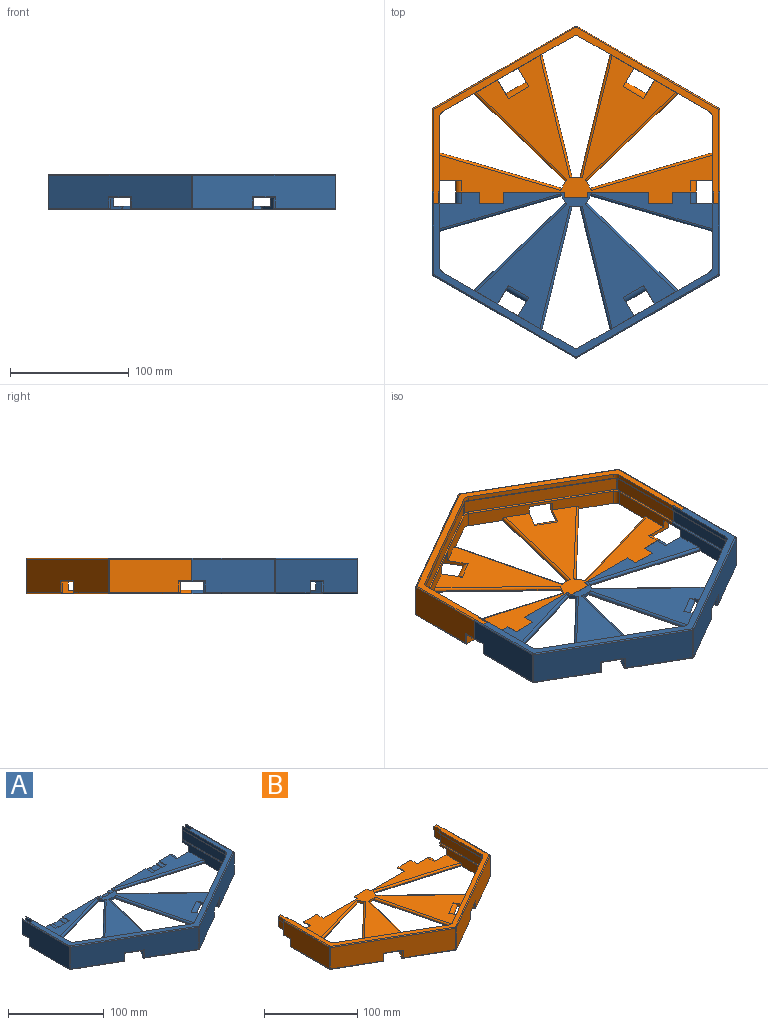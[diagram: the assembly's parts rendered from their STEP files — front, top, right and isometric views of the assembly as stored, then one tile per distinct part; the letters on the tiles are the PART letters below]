
ASSEMBLY  parts=2 mates=1
PART A: 155 faces, bbox 242.5x139.8x30 mm
  f0: plane 3.5x1.44mm, normal (0,0,1), area 1.1mm2, adj f121,f125,f126,f151
  f1: plane 3x2.31mm, normal (0,0,1), area 1.1mm2, adj f115,f122,f128,f153
  f2: plane 2.87x1.44mm, normal (0,0,-1), area 0.7mm2, adj f120,f125,f144
  f3: plane 2.5x2.08mm, normal (0,0,-1), area 0.7mm2, adj f114,f122,f146
  f4: plane 109.75x63.36mm, normal (0.5,0.87,0), area 1247.1mm2, adj f10,f14,f23,f28,f38,f39,f40,f133
  f5: plane 109.75x63.36mm, normal (-0.5,0.87,0), area 506.9mm2, adj f12,f129,f131,f145
  f6: plane 63.36x12.5mm, normal (1,0,0), area 623.6mm2, adj f7,f10,f14,f22,f36,f37,f133,f139
  f7: plane 20x6.5mm, normal (0,1,0), area 72.4mm2, adj f6,f12,f15,f18,f36,f49,f50,f51
  f8: plane 63.36x4mm, normal (-1,0,0), area 253.5mm2, adj f9,f12,f131,f147
  f9: plane 20x6.5mm, normal (0,1,0), area 72.4mm2, adj f8,f12,f16,f21,f34,f41,f42,f43
  f10: plane 229.5x114.89mm, normal (0,0,1), area 8571.3mm2, adj f4,f6,f11,f17,f21,f24,f27,f30
  f11: plane 202.49x3mm, normal (0,1,0), area 509.8mm2, adj f10,f14,f57,f58,f59,f60,f61,f62
  f12: plane 240.49x138.85mm, normal (0,0,1), area 2150.8mm2, adj f5,f7,f8,f9,f13,f15,f47,f48
  f13: plane 109.75x63.36mm, normal (0.5,0.87,0), area 506.9mm2, adj f12,f129,f130,f143
  f14: plane 240.49x138.85mm, normal (0,0,-1), area 12534mm2, adj f4,f6,f11,f17,f21,f22,f23,f24
  f15: plane 63.36x4mm, normal (1,0,0), area 253.5mm2, adj f7,f12,f130,f141
  f16: plane 69.42x28mm, normal (1,0,0), area 1833.8mm2, adj f9,f81,f82,f84,f90,f91
  f17: plane 109.75x63.36mm, normal (-0.5,0.87,0), area 1247.2mm2, adj f10,f14,f26,f29,f31,f32,f33,f132
  f18: plane 69.42x28mm, normal (-1,0,0), area 1833.8mm2, adj f7,f83,f85,f87,f88,f89
  f19: plane 120.24x69.42mm, normal (-0.5,-0.87,0), area 3667.7mm2, adj f88,f97,f98,f101,f104,f105,f107,f109
  f20: plane 120.24x69.42mm, normal (0.5,-0.87,0), area 3667.7mm2, adj f91,f92,f96,f99,f100,f103,f105,f106
  f21: plane 63.36x12.5mm, normal (-1,0,0), area 623.6mm2, adj f9,f10,f14,f25,f34,f35,f132,f136
  f22: plane 102.67x29.89mm, normal (0.28,-0.96,0), area 106.9mm2, adj f6,f14,f24,f139
  f23: plane 77.22x73.97mm, normal (-0.69,0.72,0), area 106.9mm2, adj f4,f14,f24,f140
  f24: plane 9.17x5.29mm, normal (-0.87,-0.5,0), area 21.2mm2, adj f10,f14,f22,f23,f139,f140
  f25: plane 102.67x29.89mm, normal (-0.28,-0.96,0), area 106.9mm2, adj f14,f21,f27,f136
  f26: plane 77.22x73.98mm, normal (0.69,0.72,0), area 106.9mm2, adj f14,f17,f27,f135
  f27: plane 9.17x5.29mm, normal (0.87,-0.5,0), area 21.2mm2, adj f10,f14,f25,f26,f135,f136
  f28: plane 103.86x25.46mm, normal (0.97,-0.24,0), area 106.9mm2, adj f4,f14,f30,f137
  f29: plane 103.86x25.46mm, normal (-0.97,-0.24,0), area 106.9mm2, adj f14,f17,f30,f138
  f30: plane 10.59x3mm, normal (0,-1,0), area 21.2mm2, adj f10,f14,f28,f29,f137,f138
  f31: plane 20.07x14.76mm, normal (0,0,-1), area 109.9mm2, adj f17,f32,f33,f100
  f32: plane 20.42x11.79mm, normal (0.87,0.5,0), area 99.3mm2, adj f10,f14,f17,f31,f103,f113
  f33: plane 20.42x11.79mm, normal (-0.87,-0.5,0), area 99.3mm2, adj f10,f14,f17,f31,f96,f113
  f34: plane 10x5.5mm, normal (0,0,-1), area 55mm2, adj f9,f21,f35,f81
  f35: plane 23.58x10mm, normal (0,1,0), area 99.3mm2, adj f10,f14,f21,f34,f82,f112
  f36: plane 10x5.5mm, normal (0,0,-1), area 55mm2, adj f6,f7,f37,f83
  f37: plane 23.58x10mm, normal (0,1,0), area 99.3mm2, adj f6,f10,f14,f36,f85,f111
  f38: plane 20.07x14.76mm, normal (0,0,-1), area 109.9mm2, adj f4,f39,f40,f104
  f39: plane 20.42x11.79mm, normal (0.87,-0.5,0), area 99.3mm2, adj f4,f10,f14,f38,f101,f110
  f40: plane 20.42x11.79mm, normal (-0.87,0.5,0), area 99.3mm2, adj f4,f10,f14,f38,f107,f110
  f41: plane 10x4.5mm, normal (-1,0,0), area 45mm2, adj f9,f42,f48,f90
  f42: plane 10x1mm, normal (0,0,1), area 10mm2, adj f9,f41,f43,f48
  f43: plane 10x10mm, normal (-1,0,0), area 100mm2, adj f9,f42,f44,f48
  f44: plane 10x2.5mm, normal (0,0,1), area 25mm2, adj f9,f43,f45,f48
  f45: plane 10x10mm, normal (1,0,0), area 100mm2, adj f9,f44,f46,f48
  f46: plane 10x1mm, normal (0,0,1), area 10mm2, adj f9,f45,f47,f48
  f47: plane 10x4.5mm, normal (1,0,0), area 45mm2, adj f9,f12,f46,f48
  f48: plane 14.5x4.5mm, normal (0,1,0), area 45.2mm2, adj f12,f41,f42,f43,f44,f45,f46,f47
  f49: plane 10x4.5mm, normal (-1,0,0), area 45mm2, adj f7,f12,f50,f56
  f50: plane 10x1mm, normal (0,0,1), area 10mm2, adj f7,f49,f51,f56
  f51: plane 10x10mm, normal (-1,0,0), area 100mm2, adj f7,f50,f52,f56
  f52: plane 10x2.5mm, normal (0,0,1), area 25mm2, adj f7,f51,f53,f56
  f53: plane 10x10mm, normal (1,0,0), area 100mm2, adj f7,f52,f54,f56
  f54: plane 10x1mm, normal (0,0,1), area 10mm2, adj f7,f53,f55,f56
  f55: plane 10x4.5mm, normal (1,0,0), area 45mm2, adj f7,f54,f56,f89
  f56: plane 14.5x4.5mm, normal (0,1,0), area 45.2mm2, adj f12,f49,f50,f51,f52,f53,f54,f55
  f57: plane 10x5mm, normal (0,0,1), area 50mm2, adj f11,f58,f63,f64
  f58: plane 10x1mm, normal (1,0,0), area 10mm2, adj f10,f11,f57,f64
  f59: plane 10x1mm, normal (-1,0,0), area 10mm2, adj f10,f11,f60,f64
  f60: plane 10x5mm, normal (0,0,1), area 50mm2, adj f11,f59,f61,f64
  f61: plane 10x1mm, normal (-1,0,0), area 10mm2, adj f11,f60,f62,f64
  f62: plane 10x10mm, normal (0,0,1), area 100mm2, adj f11,f61,f63,f64
  f63: plane 10x1mm, normal (1,0,0), area 10mm2, adj f11,f57,f62,f64
  f64: plane 20x2mm, normal (0,1,0), area 30mm2, adj f10,f57,f58,f59,f60,f61,f62,f63
  f65: plane 10x1mm, normal (-1,0,0), area 10mm2, adj f10,f11,f66,f72
  f66: plane 10x5mm, normal (0,0,1), area 50mm2, adj f11,f65,f67,f72
  f67: plane 10x1mm, normal (-1,0,0), area 10mm2, adj f11,f66,f68,f72
  f68: plane 10x10mm, normal (0,0,1), area 100mm2, adj f11,f67,f69,f72
  f69: plane 10x1mm, normal (1,0,0), area 10mm2, adj f11,f68,f70,f72
  f70: plane 10x5mm, normal (0,0,1), area 50mm2, adj f11,f69,f71,f72
  f71: plane 10x1mm, normal (1,0,0), area 10mm2, adj f10,f11,f70,f72
  f72: plane 20x2mm, normal (0,1,0), area 30mm2, adj f10,f65,f66,f67,f68,f69,f70,f71
  f73: plane 10x5mm, normal (0,0,1), area 50mm2, adj f11,f74,f79,f80
  f74: plane 5x1mm, normal (1,0,0), area 5mm2, adj f11,f73,f75,f80
  f75: plane 5x5mm, normal (0,0,1), area 25mm2, adj f11,f74,f76,f80
  f76: plane 5x1mm, normal (1,0,0), area 5mm2, adj f10,f11,f75,f80
  f77: plane 5x1mm, normal (-1,0,0), area 5mm2, adj f10,f11,f78,f80
  f78: plane 5x5mm, normal (0,0,1), area 25mm2, adj f11,f77,f79,f80
  f79: plane 5x1mm, normal (-1,0,0), area 5mm2, adj f11,f73,f78,f80
  f80: plane 20x2mm, normal (0,1,0), area 30mm2, adj f10,f73,f74,f75,f76,f77,f78,f79
  f81: cylinder r=1mm len=11mm, axis (0,-1,0), area 16.3mm2, adj f9,f16,f34,f82
  f82: cylinder r=1mm len=11mm, axis (0,0,-1), area 15.7mm2, adj f16,f35,f81,f84
  f83: cylinder r=1mm len=11mm, axis (0,1,0), area 16.3mm2, adj f7,f18,f36,f85
  f84: cylinder r=1mm len=59.42mm, axis (0,1,0), area 92.8mm2, adj f14,f16,f82,f86
  f85: cylinder r=1mm len=11mm, axis (0,0,1), area 15.7mm2, adj f18,f37,f83,f87
  f86: sphere r=1mm, area 1mm2, adj f84,f91,f92
  f87: cylinder r=1mm len=59.42mm, axis (0,-1,0), area 92.8mm2, adj f14,f18,f85,f93
  f88: cylinder r=1mm len=28mm, axis (0,0,-1), area 29.3mm2, adj f18,f19,f93,f94
  f89: cylinder r=1mm len=69.42mm, axis (0,1,0), area 109mm2, adj f7,f12,f18,f55,f94
  f90: cylinder r=1mm len=69.42mm, axis (0,-1,0), area 109mm2, adj f9,f12,f16,f41,f95
  f91: cylinder r=1mm len=28mm, axis (0,0,-1), area 29.3mm2, adj f16,f20,f86,f95
  f92: cylinder r=1mm len=51.96mm, axis (0.87,0.5,0), area 92.8mm2, adj f14,f20,f86,f96
  f93: sphere r=1mm, area 1mm2, adj f87,f88,f97
  f94: sphere r=1mm, area 1mm2, adj f88,f89,f98
  f95: sphere r=1mm, area 1mm2, adj f90,f91,f99
  f96: cylinder r=1mm len=11mm, axis (0,0,1), area 15.7mm2, adj f20,f33,f92,f100
  f97: cylinder r=1mm len=51.96mm, axis (0.87,-0.5,0), area 92.8mm2, adj f14,f19,f93,f101
  f98: cylinder r=1mm len=120.74mm, axis (-0.87,0.5,0), area 218.1mm2, adj f12,f19,f94,f102
  f99: cylinder r=1mm len=120.74mm, axis (-0.87,-0.5,0), area 218.1mm2, adj f12,f20,f95,f102
  f100: cylinder r=1mm len=19.55mm, axis (-0.87,-0.5,0), area 32.6mm2, adj f20,f31,f96,f103
  f101: cylinder r=1mm len=11mm, axis (0,0,-1), area 15.7mm2, adj f19,f39,f97,f104
  f102: sphere r=1mm, area 1mm2, adj f98,f99,f105
  f103: cylinder r=1mm len=11mm, axis (0,0,-1), area 15.7mm2, adj f20,f32,f100,f106
  f104: cylinder r=1mm len=19.55mm, axis (-0.87,0.5,0), area 32.6mm2, adj f19,f38,f101,f107
  f105: cylinder r=1mm len=28mm, axis (0,0,-1), area 29.3mm2, adj f19,f20,f102,f108
  f106: cylinder r=1mm len=51.96mm, axis (0.87,0.5,0), area 92.8mm2, adj f14,f20,f103,f108
  f107: cylinder r=1mm len=11mm, axis (0,0,1), area 15.7mm2, adj f19,f40,f104,f109
  f108: sphere r=1mm, area 1mm2, adj f105,f106,f109
  f109: cylinder r=1mm len=51.96mm, axis (0.87,-0.5,0), area 92.8mm2, adj f14,f19,f107,f108
  f110: cylinder r=5mm len=19.61mm, axis (-0.87,0.5,0), area 115.9mm2, adj f10,f14,f39,f40
  f111: cylinder r=5mm len=10mm, axis (0,1,0), area 58mm2, adj f10,f11,f14,f37
  f112: cylinder r=5mm len=10mm, axis (0,-1,0), area 58mm2, adj f10,f11,f14,f35
  f113: cylinder r=5mm len=19.61mm, axis (-0.87,-0.5,0), area 115.9mm2, adj f10,f14,f32,f33
  f114: plane 3.75x0.87mm, normal (0,0,-1), area 1.1mm2, adj f3,f116,f128,f146
  f115: plane 2.89x0.74mm, normal (0,0,1), area 0.7mm2, adj f1,f116,f153
  f116: plane 66.25x11.5mm, normal (-1,0,0), area 761.9mm2, adj f9,f114,f115,f128,f147,f154
  f117: plane 2.89x0.74mm, normal (0,0,-1), area 0.7mm2, adj f119,f123,f142
  f118: plane 3.75x0.87mm, normal (0,0,1), area 1.1mm2, adj f119,f124,f127,f149
  f119: plane 66.25x11.5mm, normal (1,0,0), area 761.9mm2, adj f7,f117,f118,f127,f141,f148
  f120: plane 3.5x1.44mm, normal (0,0,-1), area 1.1mm2, adj f2,f122,f126,f144
  f121: plane 2.87x1.44mm, normal (0,0,1), area 0.7mm2, adj f0,f122,f151
  f122: plane 114.75x66.25mm, normal (-0.5,0.87,0), area 1523.7mm2, adj f1,f3,f120,f121,f126,f128,f145,f152
  f123: plane 3x2.31mm, normal (0,0,-1), area 1.1mm2, adj f117,f125,f127,f142
  f124: plane 2.5x2.08mm, normal (0,0,1), area 0.7mm2, adj f118,f125,f149
  f125: plane 114.75x66.25mm, normal (0.5,0.87,0), area 1523.7mm2, adj f0,f2,f123,f124,f126,f127,f143,f150
  f126: cylinder r=2mm len=11.5mm, axis (0,0,1), area 11.6mm2, adj f0,f120,f122,f125
  f127: cylinder r=2mm len=11.5mm, axis (0,0,1), area 11.6mm2, adj f118,f119,f123,f125
  f128: cylinder r=2mm len=11.5mm, axis (0,0,1), area 11.6mm2, adj f1,f114,f116,f122
  f129: cylinder r=5mm len=5mm, axis (0,0,-1), area 20.9mm2, adj f5,f12,f13,f144
  f130: cylinder r=5mm len=4.33mm, axis (0,0,-1), area 20.9mm2, adj f12,f13,f15,f142
  f131: cylinder r=5mm len=4.33mm, axis (0,0,-1), area 20.9mm2, adj f5,f8,f12,f146
  f132: cylinder r=5mm len=12.5mm, axis (0,0,-1), area 65.4mm2, adj f14,f17,f21,f153
  f133: cylinder r=5mm len=12.5mm, axis (0,0,-1), area 65.4mm2, adj f4,f6,f14,f149
  f134: cylinder r=5mm len=12.5mm, axis (0,0,-1), area 65.4mm2, adj f4,f14,f17,f151
  f135: cylinder r=2mm len=78.6mm, axis (-0.72,0.69,0), area 334.7mm2, adj f10,f17,f26,f27
  f136: cylinder r=2mm len=103.23mm, axis (0.96,-0.28,0), area 334.7mm2, adj f10,f21,f25,f27
  f137: cylinder r=2mm len=104.34mm, axis (0.24,0.97,0), area 334.7mm2, adj f4,f10,f28,f30
  f138: cylinder r=2mm len=104.34mm, axis (0.24,-0.97,0), area 334.7mm2, adj f10,f17,f29,f30
  f139: cylinder r=2mm len=103.23mm, axis (0.96,0.28,0), area 334.7mm2, adj f6,f10,f22,f24
  f140: cylinder r=2mm len=78.61mm, axis (-0.72,-0.69,0), area 334.7mm2, adj f4,f10,f23,f24
  f141: cylinder r=1mm len=63.36mm, axis (0,-1,0), area 99.5mm2, adj f7,f15,f119,f142
  f142: torus R=6mm, axis (0,0,-1), area 8.8mm2, adj f117,f123,f130,f141,f143
  f143: cylinder r=1mm len=110.25mm, axis (0.87,-0.5,0), area 199.1mm2, adj f13,f125,f142,f144
  f144: torus R=6mm, axis (0,0,-1), area 8.8mm2, adj f2,f120,f129,f143,f145
  f145: cylinder r=1mm len=110.25mm, axis (0.87,0.5,0), area 199.1mm2, adj f5,f122,f144,f146
  f146: torus R=6mm, axis (0,0,1), area 8.8mm2, adj f3,f114,f131,f145,f147
  f147: cylinder r=1mm len=63.36mm, axis (0,1,0), area 99.5mm2, adj f8,f9,f116,f146
  f148: cylinder r=1mm len=63.36mm, axis (0,1,0), area 99.5mm2, adj f6,f7,f119,f149
  f149: torus R=6mm, axis (0,0,-1), area 8.8mm2, adj f118,f124,f133,f148,f150
  f150: cylinder r=1mm len=110.25mm, axis (-0.87,0.5,0), area 199.1mm2, adj f4,f125,f149,f151
  f151: torus R=6mm, axis (0,0,-1), area 8.8mm2, adj f0,f121,f134,f150,f152
  f152: cylinder r=1mm len=110.25mm, axis (-0.87,-0.5,0), area 199.1mm2, adj f17,f122,f151,f153
  f153: torus R=6mm, axis (0,0,1), area 8.8mm2, adj f1,f115,f132,f152,f154
  f154: cylinder r=1mm len=63.36mm, axis (0,-1,0), area 99.5mm2, adj f9,f21,f116,f153
PART B: 155 faces, bbox 242.5x149.6x30 mm
  f0: plane 3.5x1.44mm, normal (0,0,1), area 1.1mm2, adj f119,f124,f126,f151
  f1: plane 3x2.31mm, normal (0,0,1), area 1.1mm2, adj f115,f125,f128,f153
  f2: plane 2.87x1.44mm, normal (0,0,-1), area 0.7mm2, adj f119,f123,f144
  f3: plane 2.5x2.08mm, normal (0,0,-1), area 0.7mm2, adj f114,f125,f146
  f4: plane 109.75x63.36mm, normal (-0.5,0.87,0), area 1247.2mm2, adj f11,f13,f26,f29,f31,f32,f33,f132
  f5: plane 63.36x12.5mm, normal (1,0,0), area 623.6mm2, adj f6,f11,f13,f22,f36,f37,f133,f139
  f6: plane 20x6.5mm, normal (0,1,0), area 78.2mm2, adj f5,f14,f17,f20,f36,f49,f50,f51
  f7: plane 109.75x63.36mm, normal (0.5,0.87,0), area 506.9mm2, adj f20,f129,f130,f143
  f8: plane 63.36x4mm, normal (-1,0,0), area 253.5mm2, adj f9,f20,f131,f147
  f9: plane 20x6.5mm, normal (0,1,0), area 78.2mm2, adj f8,f15,f20,f21,f34,f41,f42,f43
  f10: plane 202.49x3mm, normal (0,1,0), area 512.2mm2, adj f11,f13,f57,f58,f59,f60,f61,f62
  f11: plane 229.5x124.69mm, normal (0,0,1), area 9549.6mm2, adj f4,f5,f10,f12,f21,f24,f27,f30
  f12: plane 109.75x63.36mm, normal (0.5,0.87,0), area 1247.1mm2, adj f11,f13,f23,f28,f38,f39,f40,f133
  f13: plane 240.49x138.85mm, normal (0,0,-1), area 12534mm2, adj f4,f5,f10,f12,f21,f22,f23,f24
  f14: plane 63.36x4mm, normal (1,0,0), area 253.5mm2, adj f6,f20,f130,f141
  f15: plane 69.42x28mm, normal (1,0,0), area 1833.8mm2, adj f9,f81,f82,f84,f90,f91
  f16: plane 109.75x63.36mm, normal (-0.5,0.87,0), area 506.9mm2, adj f20,f129,f131,f145
  f17: plane 69.42x28mm, normal (-1,0,0), area 1833.8mm2, adj f6,f83,f85,f87,f88,f89
  f18: plane 120.24x69.42mm, normal (-0.5,-0.87,0), area 3667.7mm2, adj f88,f97,f98,f101,f104,f105,f107,f109
  f19: plane 120.24x69.42mm, normal (0.5,-0.87,0), area 3667.7mm2, adj f91,f92,f96,f99,f100,f103,f105,f106
  f20: plane 240.49x148.65mm, normal (0,0,1), area 2320.9mm2, adj f6,f7,f8,f9,f14,f16,f41,f47
  f21: plane 63.36x12.5mm, normal (-1,0,0), area 623.6mm2, adj f9,f11,f13,f25,f34,f35,f132,f136
  f22: plane 102.67x29.89mm, normal (0.28,-0.96,0), area 106.9mm2, adj f5,f13,f24,f139
  f23: plane 77.22x73.97mm, normal (-0.69,0.72,0), area 106.9mm2, adj f12,f13,f24,f140
  f24: plane 9.17x5.29mm, normal (-0.87,-0.5,0), area 21.2mm2, adj f11,f13,f22,f23,f139,f140
  f25: plane 102.67x29.89mm, normal (-0.28,-0.96,0), area 106.9mm2, adj f13,f21,f27,f136
  f26: plane 77.22x73.98mm, normal (0.69,0.72,0), area 106.9mm2, adj f4,f13,f27,f135
  f27: plane 9.17x5.29mm, normal (0.87,-0.5,0), area 21.2mm2, adj f11,f13,f25,f26,f135,f136
  f28: plane 103.86x25.46mm, normal (0.97,-0.24,0), area 106.9mm2, adj f12,f13,f30,f137
  f29: plane 103.86x25.46mm, normal (-0.97,-0.24,0), area 106.9mm2, adj f4,f13,f30,f138
  f30: plane 10.59x3mm, normal (0,-1,0), area 21.2mm2, adj f11,f13,f28,f29,f137,f138
  f31: plane 20.07x14.76mm, normal (0,0,-1), area 109.9mm2, adj f4,f32,f33,f100
  f32: plane 20.42x11.79mm, normal (0.87,0.5,0), area 99.3mm2, adj f4,f11,f13,f31,f103,f113
  f33: plane 20.42x11.79mm, normal (-0.87,-0.5,0), area 99.3mm2, adj f4,f11,f13,f31,f96,f113
  f34: plane 10x5.5mm, normal (0,0,-1), area 55mm2, adj f9,f21,f35,f81
  f35: plane 23.58x10mm, normal (0,1,0), area 99.3mm2, adj f11,f13,f21,f34,f82,f112
  f36: plane 10x5.5mm, normal (0,0,-1), area 55mm2, adj f5,f6,f37,f83
  f37: plane 23.58x10mm, normal (0,1,0), area 99.3mm2, adj f5,f11,f13,f36,f85,f111
  f38: plane 20.07x14.76mm, normal (0,0,-1), area 109.9mm2, adj f12,f39,f40,f104
  f39: plane 20.42x11.79mm, normal (0.87,-0.5,0), area 99.3mm2, adj f11,f12,f13,f38,f101,f110
  f40: plane 20.42x11.79mm, normal (-0.87,0.5,0), area 99.3mm2, adj f11,f12,f13,f38,f107,f110
  f41: plane 9.8x4.5mm, normal (1,0,0), area 44.1mm2, adj f9,f20,f42,f48
  f42: plane 9.8x1mm, normal (0,0,-1), area 9.8mm2, adj f9,f41,f43,f48
  f43: plane 10x9.8mm, normal (1,0,0), area 98mm2, adj f9,f42,f44,f48
  f44: plane 9.8x2.1mm, normal (0,0,-1), area 20.5mm2, adj f9,f43,f45,f48
  f45: plane 10x9.8mm, normal (-1,0,0), area 98mm2, adj f9,f44,f46,f48
  f46: plane 9.8x1mm, normal (0,0,-1), area 9.8mm2, adj f9,f45,f47,f48
  f47: plane 9.8x4.5mm, normal (-1,0,0), area 44.1mm2, adj f9,f20,f46,f48
  f48: plane 14.5x4.1mm, normal (0,1,0), area 39.4mm2, adj f20,f41,f42,f43,f44,f45,f46,f47
  f49: plane 9.8x4.5mm, normal (1,0,0), area 44.1mm2, adj f6,f20,f50,f56
  f50: plane 9.8x1mm, normal (0,0,-1), area 9.8mm2, adj f6,f49,f51,f56
  f51: plane 10x9.8mm, normal (1,0,0), area 98mm2, adj f6,f50,f52,f56
  f52: plane 9.8x2.1mm, normal (0,0,-1), area 20.5mm2, adj f6,f51,f53,f56
  f53: plane 10x9.8mm, normal (-1,0,0), area 98mm2, adj f6,f52,f54,f56
  f54: plane 9.8x1mm, normal (0,0,-1), area 9.8mm2, adj f6,f53,f55,f56
  f55: plane 9.8x4.5mm, normal (-1,0,0), area 44.1mm2, adj f6,f20,f54,f56
  f56: plane 14.5x4.1mm, normal (0,1,0), area 39.4mm2, adj f20,f49,f50,f51,f52,f53,f54,f55
  f57: plane 9.8x1mm, normal (1,0,0), area 9.8mm2, adj f10,f11,f58,f64
  f58: plane 9.8x5mm, normal (0,0,-1), area 49mm2, adj f10,f57,f59,f64
  f59: plane 9.8x1mm, normal (1,0,0), area 9.8mm2, adj f10,f58,f60,f64
  f60: plane 9.8x9.6mm, normal (0,0,-1), area 94.1mm2, adj f10,f59,f61,f64
  f61: plane 9.8x1mm, normal (-1,0,0), area 9.8mm2, adj f10,f60,f62,f64
  f62: plane 9.8x5mm, normal (0,0,-1), area 49mm2, adj f10,f61,f63,f64
  f63: plane 9.8x1mm, normal (-1,0,0), area 9.8mm2, adj f10,f11,f62,f64
  f64: plane 19.6x2mm, normal (0,1,0), area 29.2mm2, adj f11,f57,f58,f59,f60,f61,f62,f63
  f65: plane 9.8x5mm, normal (0,0,-1), area 49mm2, adj f10,f66,f71,f72
  f66: plane 9.8x1mm, normal (-1,0,0), area 9.8mm2, adj f10,f11,f65,f72
  f67: plane 9.8x1mm, normal (1,0,0), area 9.8mm2, adj f10,f11,f68,f72
  f68: plane 9.8x5mm, normal (0,0,-1), area 49mm2, adj f10,f67,f69,f72
  f69: plane 9.8x1mm, normal (1,0,0), area 9.8mm2, adj f10,f68,f70,f72
  f70: plane 9.8x9.6mm, normal (0,0,-1), area 94.1mm2, adj f10,f69,f71,f72
  f71: plane 9.8x1mm, normal (-1,0,0), area 9.8mm2, adj f10,f65,f70,f72
  f72: plane 19.6x2mm, normal (0,1,0), area 29.2mm2, adj f11,f65,f66,f67,f68,f69,f70,f71
  f73: plane 9.6x4.8mm, normal (0,0,-1), area 46.1mm2, adj f10,f74,f79,f80
  f74: plane 4.8x1mm, normal (-1,0,0), area 4.8mm2, adj f10,f73,f75,f80
  f75: plane 5x4.8mm, normal (0,0,-1), area 24mm2, adj f10,f74,f76,f80
  f76: plane 4.8x1mm, normal (-1,0,0), area 4.8mm2, adj f10,f11,f75,f80
  f77: plane 4.8x1mm, normal (1,0,0), area 4.8mm2, adj f10,f11,f78,f80
  f78: plane 5x4.8mm, normal (0,0,-1), area 24mm2, adj f10,f77,f79,f80
  f79: plane 4.8x1mm, normal (1,0,0), area 4.8mm2, adj f10,f73,f78,f80
  f80: plane 19.6x2mm, normal (0,1,0), area 29.2mm2, adj f11,f73,f74,f75,f76,f77,f78,f79
  f81: cylinder r=1mm len=11mm, axis (0,-1,0), area 16.3mm2, adj f9,f15,f34,f82
  f82: cylinder r=1mm len=11mm, axis (0,0,-1), area 15.7mm2, adj f15,f35,f81,f84
  f83: cylinder r=1mm len=11mm, axis (0,1,0), area 16.3mm2, adj f6,f17,f36,f85
  f84: cylinder r=1mm len=59.42mm, axis (0,1,0), area 92.8mm2, adj f13,f15,f82,f86
  f85: cylinder r=1mm len=11mm, axis (0,0,1), area 15.7mm2, adj f17,f37,f83,f87
  f86: sphere r=1mm, area 1mm2, adj f84,f91,f92
  f87: cylinder r=1mm len=59.42mm, axis (0,-1,0), area 92.8mm2, adj f13,f17,f85,f93
  f88: cylinder r=1mm len=28mm, axis (0,0,-1), area 29.3mm2, adj f17,f18,f93,f94
  f89: cylinder r=1mm len=69.42mm, axis (0,1,0), area 109mm2, adj f6,f17,f20,f94
  f90: cylinder r=1mm len=69.42mm, axis (0,-1,0), area 109mm2, adj f9,f15,f20,f95
  f91: cylinder r=1mm len=28mm, axis (0,0,-1), area 29.3mm2, adj f15,f19,f86,f95
  f92: cylinder r=1mm len=51.96mm, axis (0.87,0.5,0), area 92.8mm2, adj f13,f19,f86,f96
  f93: sphere r=1mm, area 1mm2, adj f87,f88,f97
  f94: sphere r=1mm, area 1mm2, adj f88,f89,f98
  f95: sphere r=1mm, area 1mm2, adj f90,f91,f99
  f96: cylinder r=1mm len=11mm, axis (0,0,1), area 15.7mm2, adj f19,f33,f92,f100
  f97: cylinder r=1mm len=51.96mm, axis (0.87,-0.5,0), area 92.8mm2, adj f13,f18,f93,f101
  f98: cylinder r=1mm len=120.74mm, axis (-0.87,0.5,0), area 218.1mm2, adj f18,f20,f94,f102
  f99: cylinder r=1mm len=120.74mm, axis (-0.87,-0.5,0), area 218.1mm2, adj f19,f20,f95,f102
  f100: cylinder r=1mm len=19.55mm, axis (-0.87,-0.5,0), area 32.6mm2, adj f19,f31,f96,f103
  f101: cylinder r=1mm len=11mm, axis (0,0,-1), area 15.7mm2, adj f18,f39,f97,f104
  f102: sphere r=1mm, area 1mm2, adj f98,f99,f105
  f103: cylinder r=1mm len=11mm, axis (0,0,-1), area 15.7mm2, adj f19,f32,f100,f106
  f104: cylinder r=1mm len=19.55mm, axis (-0.87,0.5,0), area 32.6mm2, adj f18,f38,f101,f107
  f105: cylinder r=1mm len=28mm, axis (0,0,-1), area 29.3mm2, adj f18,f19,f102,f108
  f106: cylinder r=1mm len=51.96mm, axis (0.87,0.5,0), area 92.8mm2, adj f13,f19,f103,f108
  f107: cylinder r=1mm len=11mm, axis (0,0,1), area 15.7mm2, adj f18,f40,f104,f109
  f108: sphere r=1mm, area 1mm2, adj f105,f106,f109
  f109: cylinder r=1mm len=51.96mm, axis (0.87,-0.5,0), area 92.8mm2, adj f13,f18,f107,f108
  f110: cylinder r=5mm len=19.61mm, axis (-0.87,0.5,0), area 115.9mm2, adj f11,f13,f39,f40
  f111: cylinder r=5mm len=10mm, axis (0,1,0), area 58mm2, adj f10,f11,f13,f37
  f112: cylinder r=5mm len=10mm, axis (0,-1,0), area 58mm2, adj f10,f11,f13,f35
  f113: cylinder r=5mm len=19.61mm, axis (-0.87,-0.5,0), area 115.9mm2, adj f11,f13,f32,f33
  f114: plane 3.75x0.87mm, normal (0,0,-1), area 1.1mm2, adj f3,f116,f128,f146
  f115: plane 2.89x0.74mm, normal (0,0,1), area 0.7mm2, adj f1,f116,f153
  f116: plane 66.25x11.5mm, normal (-1,0,0), area 761.9mm2, adj f9,f114,f115,f128,f147,f154
  f117: plane 3x2.31mm, normal (0,0,-1), area 1.1mm2, adj f119,f120,f127,f142
  f118: plane 2.5x2.08mm, normal (0,0,1), area 0.7mm2, adj f119,f121,f149
  f119: plane 114.75x66.25mm, normal (0.5,0.87,0), area 1523.7mm2, adj f0,f2,f117,f118,f126,f127,f143,f150
  f120: plane 2.89x0.74mm, normal (0,0,-1), area 0.7mm2, adj f117,f122,f142
  f121: plane 3.75x0.87mm, normal (0,0,1), area 1.1mm2, adj f118,f122,f127,f149
  f122: plane 66.25x11.5mm, normal (1,0,0), area 761.9mm2, adj f6,f120,f121,f127,f141,f148
  f123: plane 3.5x1.44mm, normal (0,0,-1), area 1.1mm2, adj f2,f125,f126,f144
  f124: plane 2.87x1.44mm, normal (0,0,1), area 0.7mm2, adj f0,f125,f151
  f125: plane 114.75x66.25mm, normal (-0.5,0.87,0), area 1523.7mm2, adj f1,f3,f123,f124,f126,f128,f145,f152
  f126: cylinder r=2mm len=11.5mm, axis (0,0,1), area 11.6mm2, adj f0,f119,f123,f125
  f127: cylinder r=2mm len=11.5mm, axis (0,0,1), area 11.6mm2, adj f117,f119,f121,f122
  f128: cylinder r=2mm len=11.5mm, axis (0,0,1), area 11.6mm2, adj f1,f114,f116,f125
  f129: cylinder r=5mm len=5mm, axis (0,0,-1), area 20.9mm2, adj f7,f16,f20,f144
  f130: cylinder r=5mm len=4.33mm, axis (0,0,-1), area 20.9mm2, adj f7,f14,f20,f142
  f131: cylinder r=5mm len=4.33mm, axis (0,0,-1), area 20.9mm2, adj f8,f16,f20,f146
  f132: cylinder r=5mm len=12.5mm, axis (0,0,-1), area 65.4mm2, adj f4,f13,f21,f153
  f133: cylinder r=5mm len=12.5mm, axis (0,0,-1), area 65.4mm2, adj f5,f12,f13,f149
  f134: cylinder r=5mm len=12.5mm, axis (0,0,-1), area 65.4mm2, adj f4,f12,f13,f151
  f135: cylinder r=2mm len=78.6mm, axis (-0.72,0.69,0), area 334.7mm2, adj f4,f11,f26,f27
  f136: cylinder r=2mm len=103.23mm, axis (0.96,-0.28,0), area 334.7mm2, adj f11,f21,f25,f27
  f137: cylinder r=2mm len=104.34mm, axis (0.24,0.97,0), area 334.7mm2, adj f11,f12,f28,f30
  f138: cylinder r=2mm len=104.34mm, axis (0.24,-0.97,0), area 334.7mm2, adj f4,f11,f29,f30
  f139: cylinder r=2mm len=103.23mm, axis (0.96,0.28,0), area 334.7mm2, adj f5,f11,f22,f24
  f140: cylinder r=2mm len=78.61mm, axis (-0.72,-0.69,0), area 334.7mm2, adj f11,f12,f23,f24
  f141: cylinder r=1mm len=63.36mm, axis (0,-1,0), area 99.5mm2, adj f6,f14,f122,f142
  f142: torus R=6mm, axis (0,0,-1), area 8.8mm2, adj f117,f120,f130,f141,f143
  f143: cylinder r=1mm len=110.25mm, axis (0.87,-0.5,0), area 199.1mm2, adj f7,f119,f142,f144
  f144: torus R=6mm, axis (0,0,1), area 8.8mm2, adj f2,f123,f129,f143,f145
  f145: cylinder r=1mm len=110.25mm, axis (0.87,0.5,0), area 199.1mm2, adj f16,f125,f144,f146
  f146: torus R=6mm, axis (0,0,-1), area 8.8mm2, adj f3,f114,f131,f145,f147
  f147: cylinder r=1mm len=63.36mm, axis (0,1,0), area 99.5mm2, adj f8,f9,f116,f146
  f148: cylinder r=1mm len=63.36mm, axis (0,1,0), area 99.5mm2, adj f5,f6,f122,f149
  f149: torus R=6mm, axis (0,0,-1), area 8.8mm2, adj f118,f121,f133,f148,f150
  f150: cylinder r=1mm len=110.25mm, axis (-0.87,0.5,0), area 199.1mm2, adj f12,f119,f149,f151
  f151: torus R=6mm, axis (0,0,1), area 8.8mm2, adj f0,f124,f134,f150,f152
  f152: cylinder r=1mm len=110.25mm, axis (-0.87,-0.5,0), area 199.1mm2, adj f4,f125,f151,f153
  f153: torus R=6mm, axis (0,0,-1), area 8.8mm2, adj f1,f115,f132,f152,f154
  f154: cylinder r=1mm len=63.36mm, axis (0,-1,0), area 99.5mm2, adj f9,f21,f116,f153
PLACE A at identity
PLACE B rot(axis=(0,0,1),180deg) t=(0,0,0)mm
MATE slider B.f13 <-> A.f14  axis (0,0,-1) through (0,0,0)mm
